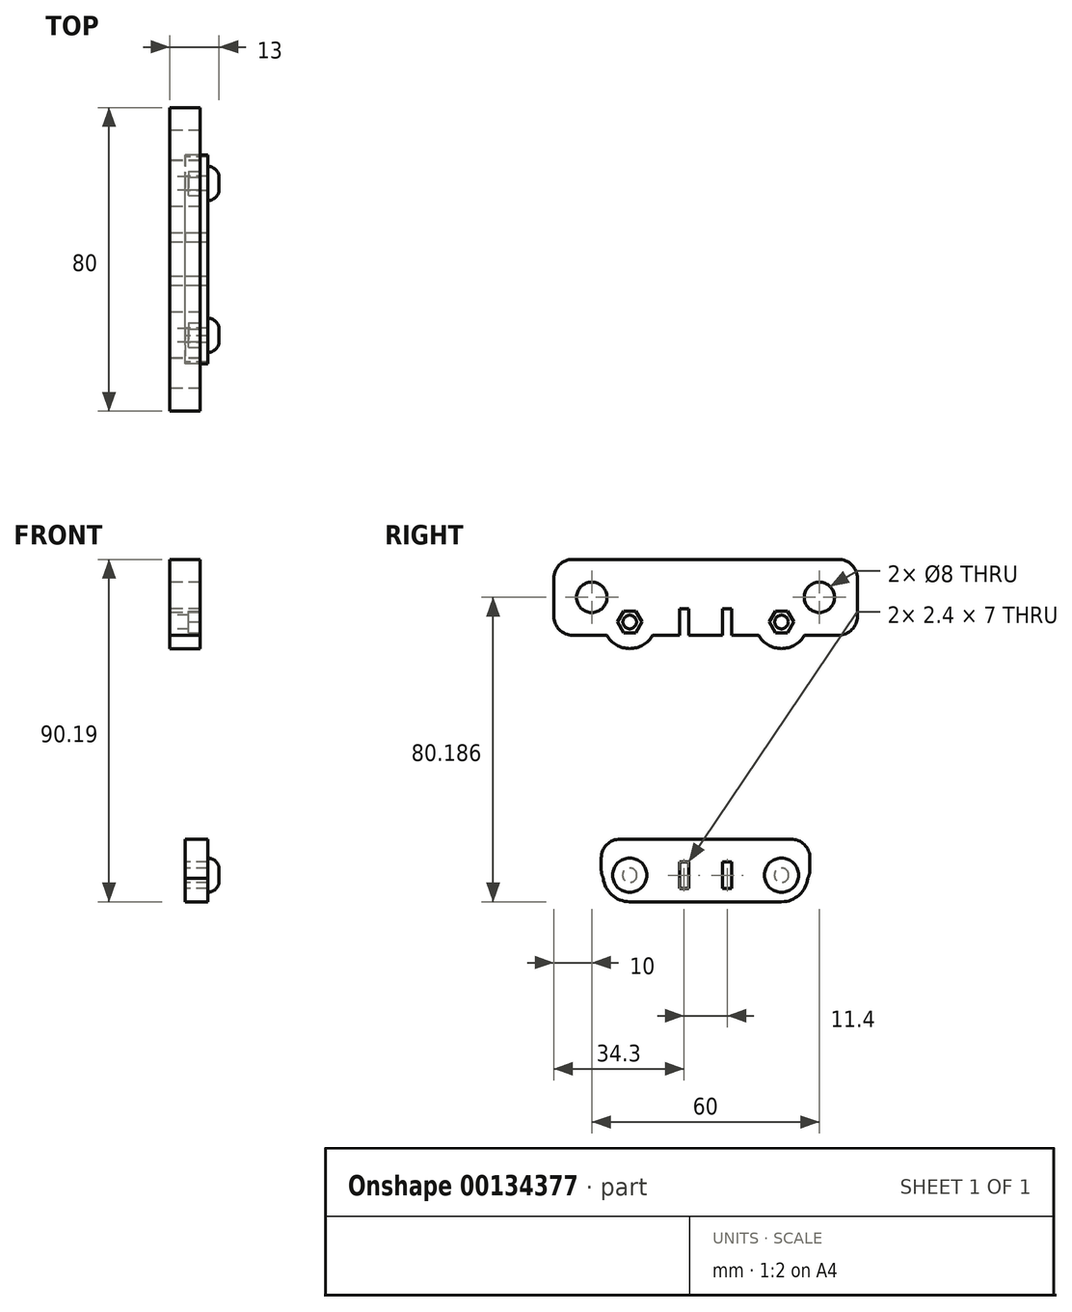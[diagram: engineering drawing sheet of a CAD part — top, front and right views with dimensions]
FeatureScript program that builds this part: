
annotation { "Feature Type Name" : "Feature", "Feature Type Description" : "" }
export const myFeature = defineFeature(function(context is Context, id is Id, definition is map)
    precondition{}
    {
        {
            var Q0;
            Q0=qCreatedBy(makeId("Right.planeOp"),FACE);
            var sketch = newSketch(context, id + "F0", { "sketchPlane" : qUnion([Q0])});
            skLineSegment(sketch, "E0", {"start": v(0, 142.5) * mm, "end": v(0, -139.74) * mm, "construction": true});
            skLineSegment(sketch, "E1.bottom", {"start": v(-35, 25) * mm, "end": v(35, 25) * mm});
            skLineSegment(sketch, "E1.top", {"start": v(-40, -25) * mm, "end": v(40, -25) * mm});
            skLineSegment(sketch, "E1.left", {"start": v(-40, 20) * mm, "end": v(-40, -25) * mm});
            skLineSegment(sketch, "E1.right", {"start": v(40, 20) * mm, "end": v(40, -25) * mm});
            skPoint(sketch, "E1.middle", {"position": v(0, 0) * mm});
            skCircle(sketch, "E2", {"center": v(-30, 13) * mm, "radius": 4 * mm});
            skCircle(sketch, "E3", {"center": v(30, 13) * mm, "radius": 4 * mm});
            skCircle(sketch, "E4", {"center": v(-30, -13) * mm, "radius": 5 * mm});
            skCircle(sketch, "E5", {"center": v(30, -13) * mm, "radius": 5 * mm});
            skPoint(sketch, "E6.visualSharp", {"position": v(-40, 25) * mm});
            skArc(sketch, "E6.filletArc", {"start": v(-35, 25) * mm, "mid": v(-38.54, 23.54) * mm, "end": v(-40, 20) * mm});
            skPoint(sketch, "E7.visualSharp", {"position": v(40, 25) * mm});
            skArc(sketch, "E7.filletArc", {"start": v(40, 20) * mm, "mid": v(38.54, 23.54) * mm, "end": v(35, 25) * mm});
            skLineSegment(sketch, "E8.bottom", {"start": v(-11, 25) * mm, "end": v(11, 25) * mm});
            skLineSegment(sketch, "E8.top", {"start": v(-9, 8) * mm, "end": v(9, 8) * mm});
            skLineSegment(sketch, "E8.left", {"start": v(-11, 25) * mm, "end": v(-11, 10) * mm});
            skLineSegment(sketch, "E8.right", {"start": v(11, 25) * mm, "end": v(11, 10) * mm});
            skPoint(sketch, "E8.middle", {"position": v(0, 16.5) * mm});
            skPoint(sketch, "E9.visualSharp", {"position": v(11, 8) * mm});
            skArc(sketch, "E9.filletArc", {"start": v(9, 8) * mm, "mid": v(10.41, 8.59) * mm, "end": v(11, 10) * mm});
            skPoint(sketch, "E10.visualSharp", {"position": v(-11, 8) * mm});
            skArc(sketch, "E10.filletArc", {"start": v(-11, 10) * mm, "mid": v(-10.41, 8.59) * mm, "end": v(-9, 8) * mm});
            skSolve(sketch);
        }
        {
            var Q0;
            Q0=makeQuery(id+"F0.imprint","IMPRINT",FACE,{"disambiguationData":[TD([[makeQuery(id+"F0.imprint","IMPRINT",EDGE,{"derivedFrom":sQuery(id+"F0.wireOp",EDGE,"E1.bottom")}),-1.0]])]});
            extrude(context, id + "F1", {"entities" : qUnion([Q0]), "endBound" : BoundingType.SYMMETRIC, "depth" : 8 * mm});
        }
        {
            var Q0;
            {var subQ0=sQuery(id+"F0.wireOp",EDGE,"E1.bottom");Q0=makeQuery(id+"F1.opExtrude","SWEPT_FACE",FACE,{"disambiguationData":[OSD([subQ0]),TDD([makeQuery(id+"F0.imprint","IMPRINT",EDGE,{"disambiguationData":[TD([[makeQuery(id+"F0.imprint","INTERSECT",VERTEX,{"derivedFrom":[subQ0,sQuery(id+"F0.wireOp",EDGE,"E7.filletArc")]}),1.0]])],"derivedFrom":subQ0})])]});}
            var sketch = newSketch(context, id + "F2", { "sketchPlane" : qUnion([Q0])});
            skCircle(sketch, "E11", {"center": v(0, 30) * mm, "radius": 1.4 * mm});
            skCircle(sketch, "E12", {"center": v(0, 24) * mm, "radius": 1.4 * mm});
            skCircle(sketch, "E13", {"center": v(0, -24) * mm, "radius": 1.4 * mm});
            skCircle(sketch, "E14", {"center": v(0, -30) * mm, "radius": 1.4 * mm});
            skLineSegment(sketch, "E15", {"start": v(-76.86, 0) * mm, "end": v(82.98, 0) * mm, "construction": true});
            skSolve(sketch);
        }
        {
            var Q0;
            Q0=qSketchRegion(id+"F2",true);
            extrude(context, id + "F3", {"entities" : qUnion([Q0]), "operationType" : NewBodyOperationType.REMOVE, "oppositeDirection" : true, "depth" : 13 * mm});
        }
        {
            var Q0;
            Q0=qCreatedBy(makeId("Right.planeOp"),FACE);
            var sketch = newSketch(context, id + "F4", { "sketchPlane" : qUnion([Q0])});
            skLineSegment(sketch, "E16", {"start": v(0, 90) * mm, "end": v(0, 27.03) * mm, "construction": true});
            skCircle(sketch, "E17", {"center": v(-30, 70.19) * mm, "radius": 4 * mm});
            skCircle(sketch, "E18", {"center": v(30, 70.19) * mm, "radius": 4 * mm});
            skLineSegment(sketch, "E19.bottom", {"start": v(-35, 80.19) * mm, "end": v(35, 80.19) * mm});
            skLineSegment(sketch, "E19.top", {"start": v(-35, 60.19) * mm, "end": v(-26.06, 60.19) * mm});
            skLineSegment(sketch, "E19.left", {"start": v(-40, 75.19) * mm, "end": v(-40, 65.19) * mm});
            skLineSegment(sketch, "E19.right", {"start": v(40, 75.19) * mm, "end": v(40, 65.19) * mm});
            skPoint(sketch, "E19.middle", {"position": v(0, 70.19) * mm});
            skPoint(sketch, "E20.visualSharp", {"position": v(-40, 80.19) * mm});
            skArc(sketch, "E20.filletArc", {"start": v(-35, 80.19) * mm, "mid": v(-38.54, 78.72) * mm, "end": v(-40, 75.19) * mm});
            skPoint(sketch, "E21.visualSharp", {"position": v(-40, 60.19) * mm});
            skArc(sketch, "E21.filletArc", {"start": v(-40, 65.19) * mm, "mid": v(-38.54, 61.65) * mm, "end": v(-35, 60.19) * mm});
            skPoint(sketch, "E22.visualSharp", {"position": v(40, 80.19) * mm});
            skArc(sketch, "E22.filletArc", {"start": v(40, 75.19) * mm, "mid": v(38.54, 78.72) * mm, "end": v(35, 80.19) * mm});
            skPoint(sketch, "E23.visualSharp", {"position": v(40, 60.19) * mm});
            skArc(sketch, "E23.filletArc", {"start": v(35, 60.19) * mm, "mid": v(38.54, 61.65) * mm, "end": v(40, 65.19) * mm});
            skLineSegment(sketch, "E24.bottom", {"start": v(-11, 80.19) * mm, "end": v(11, 80.19) * mm});
            skPoint(sketch, "E24.middle", {"position": v(0, 76.69) * mm});
            skLineSegment(sketch, "E25", {"start": v(-87.97, 70.19) * mm, "end": v(-87.97, 70.19) * mm});
            skPoint(sketch, "E25.endSnap0", {"position": v(40, 70.19) * mm});
            skLineSegment(sketch, "E26.bottom", {"start": v(-6.9, 67.19) * mm, "end": v(-4.5, 67.19) * mm});
            skLineSegment(sketch, "E26.top", {"start": v(-6.9, 60.19) * mm, "end": v(-4.5, 60.19) * mm});
            skLineSegment(sketch, "E26.left", {"start": v(-6.9, 67.19) * mm, "end": v(-6.9, 60.19) * mm});
            skLineSegment(sketch, "E26.right", {"start": v(-4.5, 67.19) * mm, "end": v(-4.5, 60.19) * mm});
            skLineSegment(sketch, "E27.bottom", {"start": v(4.5, 67.19) * mm, "end": v(6.9, 67.19) * mm});
            skLineSegment(sketch, "E27.top", {"start": v(4.5, 60.19) * mm, "end": v(6.9, 60.19) * mm});
            skLineSegment(sketch, "E27.left", {"start": v(4.5, 67.19) * mm, "end": v(4.5, 60.19) * mm});
            skLineSegment(sketch, "E27.right", {"start": v(6.9, 67.19) * mm, "end": v(6.9, 60.19) * mm});
            skCircle(sketch, "E28", {"center": v(-20, 63.69) * mm, "radius": 1.8 * mm});
            skCircle(sketch, "E29", {"center": v(20, 63.69) * mm, "radius": 1.8 * mm});
            skArc(sketch, "E30", {"start": v(-26.06, 60.19) * mm, "mid": v(-20, 56.69) * mm, "end": v(-13.94, 60.19) * mm});
            skArc(sketch, "E31.MirrorC", {"start": v(26.06, 60.19) * mm, "mid": v(20, 56.69) * mm, "end": v(13.94, 60.19) * mm});
            skLineSegment(sketch, "E32.trimOffspring", {"start": v(-13.94, 60.19) * mm, "end": v(13.94, 60.19) * mm});
            skLineSegment(sketch, "E33.trimOffspring", {"start": v(26.06, 60.19) * mm, "end": v(35, 60.19) * mm});
            skSolve(sketch);
        }
        {
            var Q0;
            Q0=makeQuery(id+"F4.imprint","IMPRINT",FACE,{"disambiguationData":[TD([[makeQuery(id+"F4.imprint","IMPRINT",EDGE,{"derivedFrom":sQuery(id+"F4.wireOp",EDGE,"E17")}),-1.0]])]});
            extrude(context, id + "F5", {"entities" : qUnion([Q0]), "endBound" : BoundingType.SYMMETRIC, "depth" : 8 * mm});
        }
        {
            var Q0;
            Q0=makeQuery(id+"F5.opExtrude","CAP_FACE",FACE,{"disambiguationData":[OSD([sQuery(id+"F4.wireOp",EDGE,"E17"),sQuery(id+"F4.wireOp",EDGE,"E18"),sQuery(id+"F4.wireOp",EDGE,"E19.bottom"),sQuery(id+"F4.wireOp",EDGE,"E19.top"),sQuery(id+"F4.wireOp",EDGE,"E19.left"),sQuery(id+"F4.wireOp",EDGE,"E19.right"),sQuery(id+"F4.wireOp",EDGE,"E20.filletArc"),sQuery(id+"F4.wireOp",EDGE,"E21.filletArc"),sQuery(id+"F4.wireOp",EDGE,"E22.filletArc"),sQuery(id+"F4.wireOp",EDGE,"E23.filletArc"),sQuery(id+"F4.wireOp",EDGE,"E24.bottom"),sQuery(id+"F4.wireOp",EDGE,"E26.bottom"),sQuery(id+"F4.wireOp",EDGE,"E26.left"),sQuery(id+"F4.wireOp",EDGE,"E26.right"),sQuery(id+"F4.wireOp",EDGE,"E27.bottom"),sQuery(id+"F4.wireOp",EDGE,"E27.left"),sQuery(id+"F4.wireOp",EDGE,"E27.right"),sQuery(id+"F4.wireOp",EDGE,"E28"),sQuery(id+"F4.wireOp",EDGE,"E29")])],"isStart":false});
            var sketch = newSketch(context, id + "F6", { "sketchPlane" : qUnion([Q0])});
            skCircle(sketch, "E34.cCircle", {"center": v(20, 63.69) * mm, "radius": 2.8 * mm, "construction": true});
            skLineSegment(sketch, "E34.0", {"start": v(18.38, 66.49) * mm, "end": v(21.62, 66.49) * mm});
            skLineSegment(sketch, "E34.1", {"start": v(21.62, 66.49) * mm, "end": v(23.23, 63.69) * mm});
            skLineSegment(sketch, "E34.2", {"start": v(23.23, 63.69) * mm, "end": v(21.62, 60.89) * mm});
            skLineSegment(sketch, "E34.3", {"start": v(21.62, 60.89) * mm, "end": v(18.38, 60.89) * mm});
            skLineSegment(sketch, "E34.4", {"start": v(18.38, 60.89) * mm, "end": v(16.77, 63.69) * mm});
            skLineSegment(sketch, "E34.5", {"start": v(16.77, 63.69) * mm, "end": v(18.38, 66.49) * mm});
            skPoint(sketch, "E34.0.midPoint", {"position": v(20, 66.49) * mm});
            skCircle(sketch, "E35.cCircle", {"center": v(-20, 63.69) * mm, "radius": 2.8 * mm, "construction": true});
            skLineSegment(sketch, "E35.0", {"start": v(-21.62, 66.49) * mm, "end": v(-18.38, 66.49) * mm});
            skLineSegment(sketch, "E35.1", {"start": v(-18.38, 66.49) * mm, "end": v(-16.77, 63.69) * mm});
            skLineSegment(sketch, "E35.2", {"start": v(-16.77, 63.69) * mm, "end": v(-18.38, 60.89) * mm});
            skLineSegment(sketch, "E35.3", {"start": v(-18.38, 60.89) * mm, "end": v(-21.62, 60.89) * mm});
            skLineSegment(sketch, "E35.4", {"start": v(-21.62, 60.89) * mm, "end": v(-23.23, 63.69) * mm});
            skLineSegment(sketch, "E35.5", {"start": v(-23.23, 63.69) * mm, "end": v(-21.62, 66.49) * mm});
            skPoint(sketch, "E35.0.midPoint", {"position": v(-20, 66.49) * mm});
            skSolve(sketch);
        }
        {
            var Q0;
            Q0=qSketchRegion(id+"F6",true);
            extrude(context, id + "F7", {"entities" : qUnion([Q0]), "operationType" : NewBodyOperationType.REMOVE, "oppositeDirection" : true, "depth" : 3 * mm});
        }
        {
            var Q0;
            Q0=qCreatedBy(makeId("Right.planeOp"),FACE);
            var sketch = newSketch(context, id + "F8", { "sketchPlane" : qUnion([Q0])});
            skLineSegment(sketch, "E36.bottom", {"start": v(-22.5, 6.5) * mm, "end": v(22.5, 6.5) * mm});
            skLineSegment(sketch, "E36.top", {"start": v(-6.9, -6.5) * mm, "end": v(-4.5, -6.5) * mm});
            skLineSegment(sketch, "E36.left", {"start": v(-27.5, 1.5) * mm, "end": v(-27.5, -1.5) * mm});
            skLineSegment(sketch, "E36.right", {"start": v(27.5, 1.5) * mm, "end": v(27.5, -1.5) * mm});
            skPoint(sketch, "E36.middle", {"position": v(0, 0) * mm});
            skPoint(sketch, "E37.visualSharp", {"position": v(-27.5, 6.5) * mm});
            skArc(sketch, "E37.filletArc", {"start": v(-22.5, 6.5) * mm, "mid": v(-26.04, 5.04) * mm, "end": v(-27.5, 1.5) * mm});
            skPoint(sketch, "E38.visualSharp", {"position": v(-27.5, -6.5) * mm});
            skArc(sketch, "E38.filletArc", {"start": v(-27.5, -1.5) * mm, "mid": v(-27.36, -2.66) * mm, "end": v(-26.96, -3.76) * mm});
            skPoint(sketch, "E39.visualSharp", {"position": v(27.5, 6.5) * mm});
            skArc(sketch, "E39.filletArc", {"start": v(27.5, 1.5) * mm, "mid": v(26.04, 5.04) * mm, "end": v(22.5, 6.5) * mm});
            skPoint(sketch, "E40.visualSharp", {"position": v(27.5, -6.5) * mm});
            skArc(sketch, "E40.filletArc", {"start": v(26.96, -3.76) * mm, "mid": v(27.36, -2.66) * mm, "end": v(27.5, -1.5) * mm});
            skLineSegment(sketch, "E41.bottom", {"start": v(-6.9, 0.5) * mm, "end": v(-4.5, 0.5) * mm});
            skLineSegment(sketch, "E41.left", {"start": v(-6.9, 0.5) * mm, "end": v(-6.9, -6.5) * mm});
            skLineSegment(sketch, "E41.right", {"start": v(-4.5, 0.5) * mm, "end": v(-4.5, -6.5) * mm});
            skLineSegment(sketch, "E42.MirrorCS", {"start": v(6.9, 0.5) * mm, "end": v(4.5, 0.5) * mm});
            skLineSegment(sketch, "E43.MirrorCS", {"start": v(6.9, -6.5) * mm, "end": v(4.5, -6.5) * mm});
            skLineSegment(sketch, "E44.MirrorCS", {"start": v(4.5, 0.5) * mm, "end": v(4.5, -6.5) * mm});
            skLineSegment(sketch, "E45.MirrorCS", {"start": v(6.9, 0.5) * mm, "end": v(6.9, -6.5) * mm});
            skCircle(sketch, "E46", {"center": v(20, -3) * mm, "radius": 1.9 * mm});
            skCircle(sketch, "E47.MirrorC", {"center": v(-20, -3) * mm, "radius": 1.9 * mm});
            skArc(sketch, "E48", {"start": v(-26.96, -3.76) * mm, "mid": v(-24.64, -8.24) * mm, "end": v(-19.91, -10) * mm});
            skArc(sketch, "E49.MirrorC", {"start": v(26.96, -3.76) * mm, "mid": v(24.67, -8.21) * mm, "end": v(20, -10) * mm});
            skPoint(sketch, "E50.orphan", {"position": v(22.5, -6.5) * mm});
            skLineSegment(sketch, "E51", {"start": v(-20.09, -10) * mm, "end": v(20, -10) * mm});
            skLineSegment(sketch, "E52.trimOffspring", {"start": v(4.5, -6.5) * mm, "end": v(6.9, -6.5) * mm});
            skSolve(sketch);
        }
        {
            var Q0;
            Q0=makeQuery(id+"F8.imprint","IMPRINT",FACE,{"disambiguationData":[TD([[makeQuery(id+"F8.imprint","IMPRINT",EDGE,{"derivedFrom":sQuery(id+"F8.wireOp",EDGE,"E36.bottom")}),-1.0]])]});
            extrude(context, id + "F9", {"entities" : qUnion([Q0]), "depth" : 6 * mm});
        }
        {
            var Q0;
            Q0=makeQuery(id+"F1.opExtrude","SWEPT_BODY",BODY,{"disambiguationData":[OSD([sQuery(id+"F0.wireOp",EDGE,"E1.bottom"),sQuery(id+"F0.wireOp",EDGE,"E1.top"),sQuery(id+"F0.wireOp",EDGE,"E1.left"),sQuery(id+"F0.wireOp",EDGE,"E1.right"),sQuery(id+"F0.wireOp",EDGE,"E2"),sQuery(id+"F0.wireOp",EDGE,"E3"),sQuery(id+"F0.wireOp",EDGE,"E4"),sQuery(id+"F0.wireOp",EDGE,"E5"),sQuery(id+"F0.wireOp",EDGE,"E6.filletArc"),sQuery(id+"F0.wireOp",EDGE,"E7.filletArc"),sQuery(id+"F0.wireOp",EDGE,"E8.top"),sQuery(id+"F0.wireOp",EDGE,"E8.left"),sQuery(id+"F0.wireOp",EDGE,"E8.right"),sQuery(id+"F0.wireOp",EDGE,"E9.filletArc"),sQuery(id+"F0.wireOp",EDGE,"E10.filletArc")])]});
            deleteBodies(context, id + "F10", {"entities" : qUnion([Q0])});
        }
        {
            var Q0;
            Q0=makeQuery(id+"F9.opExtrude","CAP_FACE",FACE,{"disambiguationData":[OSD([sQuery(id+"F8.wireOp",EDGE,"E36.bottom"),sQuery(id+"F8.wireOp",EDGE,"E36.top"),sQuery(id+"F8.wireOp",EDGE,"E36.left"),sQuery(id+"F8.wireOp",EDGE,"E36.right"),sQuery(id+"F8.wireOp",EDGE,"E37.filletArc"),sQuery(id+"F8.wireOp",EDGE,"E38.filletArc"),sQuery(id+"F8.wireOp",EDGE,"E39.filletArc"),sQuery(id+"F8.wireOp",EDGE,"E40.filletArc"),sQuery(id+"F8.wireOp",EDGE,"E41.bottom"),sQuery(id+"F8.wireOp",EDGE,"E41.left"),sQuery(id+"F8.wireOp",EDGE,"E41.right"),sQuery(id+"F8.wireOp",EDGE,"E42.MirrorCS"),sQuery(id+"F8.wireOp",EDGE,"E44.MirrorCS"),sQuery(id+"F8.wireOp",EDGE,"E45.MirrorCS"),sQuery(id+"F8.wireOp",EDGE,"E46"),sQuery(id+"F8.wireOp",EDGE,"E47.MirrorC")])],"isStart":false});
            var sketch = newSketch(context, id + "F11", { "sketchPlane" : qUnion([Q0])});
            skCircle(sketch, "E53", {"center": v(-20, -3) * mm, "radius": 4.5 * mm});
            skCircle(sketch, "E54.MirrorC", {"center": v(20, -3) * mm, "radius": 4.5 * mm});
            skSolve(sketch);
        }
        {
            var Q0;
            Q0=qSketchRegion(id+"F11",true);
            extrude(context, id + "F12", {"entities" : qUnion([Q0]), "operationType" : NewBodyOperationType.ADD, "depth" : 3 * mm});
        }
        {
            var Q0;
            Q0=makeQuery(id+"F12.opExtrude","CAP_EDGE",EDGE,{"disambiguationData":[OSD([sQuery(id+"F11.wireOp",EDGE,"E53")])],"isStart":false});
            var Q1;
            Q1=makeQuery(id+"F12.opExtrude","CAP_EDGE",EDGE,{"disambiguationData":[OSD([sQuery(id+"F11.wireOp",EDGE,"E54.MirrorC")])],"isStart":false});
            fillet(context, id + "F13", {"entities" : qUnion([Q0, Q1]), "radius" : 3 * mm, "tangentPropagation" : true, "allowEdgeOverflow" : false});
        }
    });
